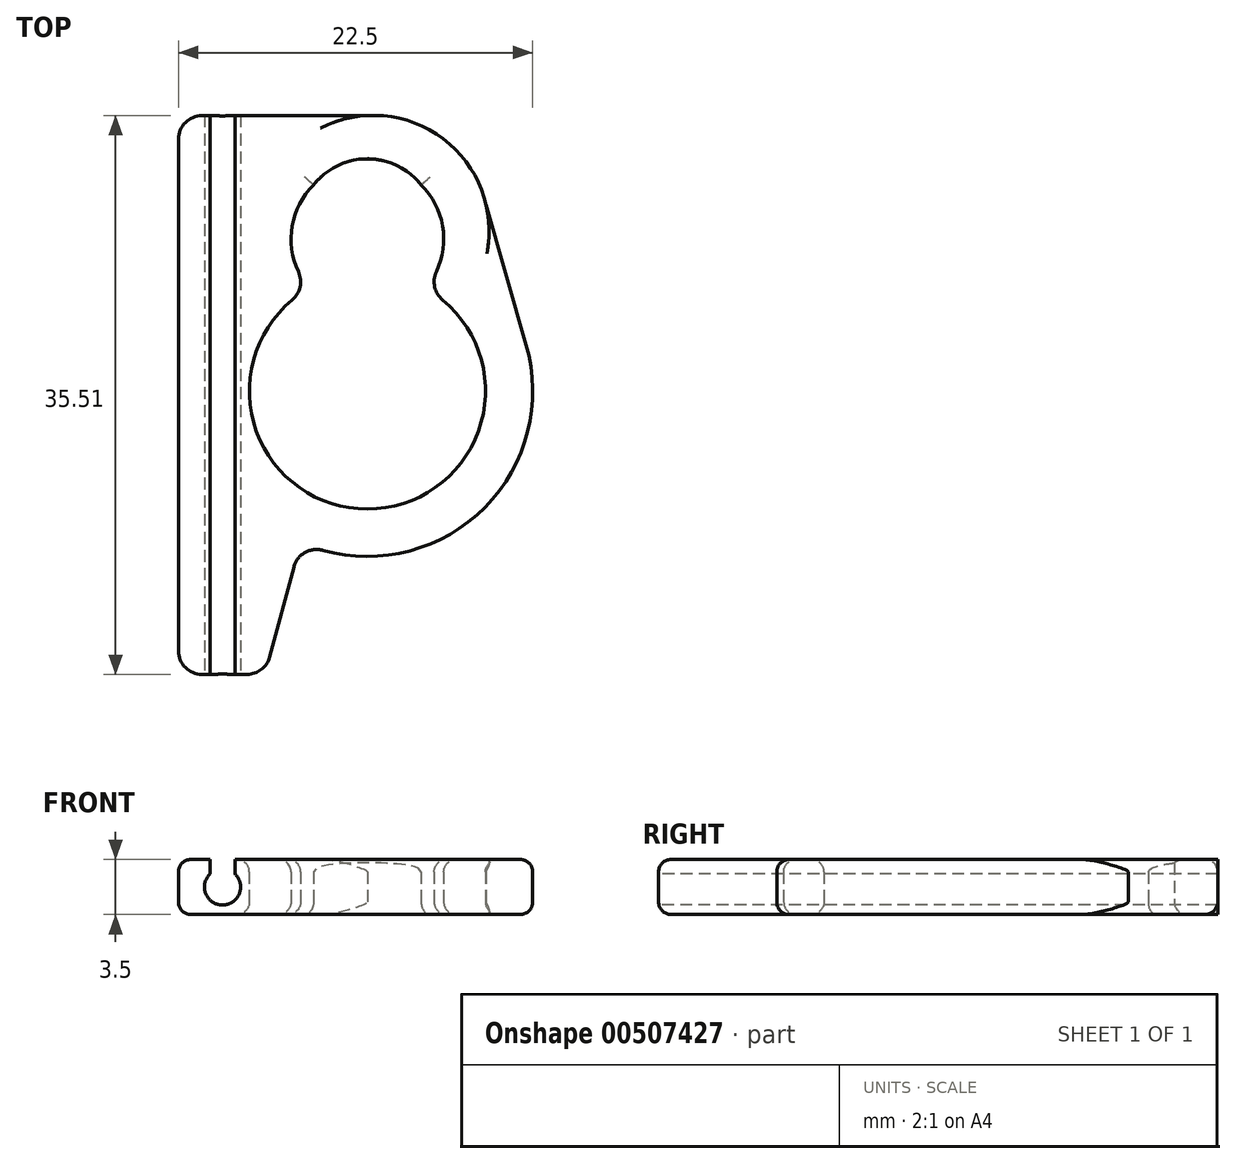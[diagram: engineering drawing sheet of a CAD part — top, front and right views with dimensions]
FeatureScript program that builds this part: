
annotation { "Feature Type Name" : "Feature", "Feature Type Description" : "" }
export const myFeature = defineFeature(function(context is Context, id is Id, definition is map)
    precondition{}
    {
        {
            var Q0;
            Q0=qCreatedBy(makeId("Top.planeOp"),FACE);
            var sketch = newSketch(context, id + "F0", { "sketchPlane" : qUnion([Q0])});
            skArc(sketch, "E0", {"start": v(-3.7, 6.52) * mm, "mid": v(0, -7.5) * mm, "end": v(3.7, 6.52) * mm});
            skArc(sketch, "E1", {"start": v(3.7, 6.52) * mm, "mid": v(0, 14.5) * mm, "end": v(-3.7, 6.52) * mm});
            skArc(sketch, "E2.0", {"start": v(7.54, 11.84) * mm, "mid": v(4.71, 15.93) * mm, "end": v(0, 17.5) * mm});
            skArc(sketch, "E2.1", {"start": v(-4.25, -9.6) * mm, "mid": v(6.91, -7.9) * mm, "end": v(10.08, 2.93) * mm});
            skPoint(sketch, "E3.endSnap0", {"position": v(0, -7.5) * mm});
            skLineSegment(sketch, "E4.MirrorCS", {"start": v(10.08, 2.93) * mm, "end": v(7.54, 11.84) * mm});
            skArc(sketch, "E5.MirrorCS", {"start": v(0, 17.5) * mm, "mid": v(4.8, 16.04) * mm, "end": v(7.54, 11.84) * mm});
            skArc(sketch, "E6.MirrorCS", {"start": v(-2.47, 6.82) * mm, "mid": v(0, 14.75) * mm, "end": v(2.47, 6.82) * mm});
            skLineSegment(sketch, "E7", {"start": v(0, 17.5) * mm, "end": v(-12, 17.5) * mm});
            skLineSegment(sketch, "E8", {"start": v(-12, 17.5) * mm, "end": v(-12, -18) * mm});
            skLineSegment(sketch, "E9", {"start": v(-12, -18) * mm, "end": v(-6.5, -18) * mm});
            skLineSegment(sketch, "E10", {"start": v(-6.5, -18) * mm, "end": v(-4.25, -9.6) * mm});
            skSolve(sketch);
        }
        {
            var Q0;
            Q0=qSketchRegion(id+"F0",true);
            extrude(context, id + "F1", {"entities" : qUnion([Q0]), "depth" : 3.5 * mm});
        }
        {
            var Q0;
            Q0=makeQuery(id+"F1.opExtrude","SWEPT_EDGE",EDGE,{"disambiguationData":[OSD([sQuery(id+"F0.wireOp",EDGE,"E9"),sQuery(id+"F0.wireOp",EDGE,"E10")])]});
            var Q1;
            Q1=makeQuery(id+"F1.opExtrude","SWEPT_EDGE",EDGE,{"disambiguationData":[OSD([sQuery(id+"F0.wireOp",EDGE,"E8"),sQuery(id+"F0.wireOp",EDGE,"E9")])]});
            var Q2;
            Q2=makeQuery(id+"F1.opExtrude","SWEPT_EDGE",EDGE,{"disambiguationData":[OSD([sQuery(id+"F0.wireOp",EDGE,"E2.1"),sQuery(id+"F0.wireOp",EDGE,"E10")])]});
            var Q3;
            {var subQ0=sQuery(id+"F0.wireOp",EDGE,"E6.MirrorCS");var subQ1=sQuery(id+"F0.wireOp",EDGE,"E0");Q3=makeQuery(id+"F1.opExtrude","SWEPT_EDGE",EDGE,{"disambiguationData":[OSD([subQ1,subQ0]),TDD([makeQuery(id+"F0.imprint","INTERSECT",VERTEX,{"disambiguationData":[OD(0.0)],"derivedFrom":[subQ1,subQ0]})])]});}
            var Q4;
            {var subQ0=sQuery(id+"F0.wireOp",EDGE,"E6.MirrorCS");var subQ1=sQuery(id+"F0.wireOp",EDGE,"E0");Q4=makeQuery(id+"F1.opExtrude","SWEPT_EDGE",EDGE,{"disambiguationData":[OSD([subQ1,subQ0]),TDD([makeQuery(id+"F0.imprint","INTERSECT",VERTEX,{"disambiguationData":[OD(1.0)],"derivedFrom":[subQ1,subQ0]})])]});}
            var Q5;
            Q5=makeQuery(id+"F1.opExtrude","SWEPT_EDGE",EDGE,{"disambiguationData":[OSD([sQuery(id+"F0.wireOp",EDGE,"E7"),sQuery(id+"F0.wireOp",EDGE,"E8")])]});
            var Q6;
            {var subQ0=sQuery(id+"F0.wireOp",EDGE,"E1");var subQ1=sQuery(id+"F0.wireOp",EDGE,"E0");Q6=makeQuery(id+"F1.opExtrude","SWEPT_EDGE",EDGE,{"disambiguationData":[OSD([subQ1,subQ0]),TDD([makeQuery(id+"F0.imprint","INTERSECT",VERTEX,{"disambiguationData":[OD(0.0)],"derivedFrom":[subQ1,subQ0]})])]});}
            var Q7;
            {var subQ0=sQuery(id+"F0.wireOp",EDGE,"E1");var subQ1=sQuery(id+"F0.wireOp",EDGE,"E0");Q7=makeQuery(id+"F1.opExtrude","SWEPT_EDGE",EDGE,{"disambiguationData":[OSD([subQ1,subQ0]),TDD([makeQuery(id+"F0.imprint","INTERSECT",VERTEX,{"disambiguationData":[OD(1.0)],"derivedFrom":[subQ1,subQ0]})])]});}
            fillet(context, id + "F2", {"entities" : qUnion([Q0, Q1, Q2, Q3, Q4, Q5, Q6, Q7]), "radius" : 1.5 * mm, "tangentPropagation" : true, "allowEdgeOverflow" : false});
        }
        {
            var Q0;
            Q0=makeQuery(id+"F1.opExtrude","CAP_EDGE",EDGE,{"disambiguationData":[OSD([sQuery(id+"F0.wireOp",EDGE,"E8")])],"isStart":false});
            var Q1;
            Q1=makeQuery(id+"F1.opExtrude","CAP_EDGE",EDGE,{"disambiguationData":[OSD([sQuery(id+"F0.wireOp",EDGE,"E0")])],"isStart":false});
            var Q2;
            Q2=makeQuery(id+"F1.opExtrude","CAP_EDGE",EDGE,{"disambiguationData":[OSD([sQuery(id+"F0.wireOp",EDGE,"E4.MirrorCS")])],"isStart":true});
            var Q3;
            Q3=makeQuery(id+"F1.opExtrude","CAP_EDGE",EDGE,{"disambiguationData":[OSD([sQuery(id+"F0.wireOp",EDGE,"E6.MirrorCS")])],"isStart":true});
            var Q4;
            Q4=makeQuery(id+"F1.opExtrude","CAP_EDGE",EDGE,{"disambiguationData":[OSD([sQuery(id+"F0.wireOp",EDGE,"E9")])],"isStart":true});
            var Q5;
            Q5=makeQuery(id+"F1.opExtrude","CAP_EDGE",EDGE,{"disambiguationData":[OSD([sQuery(id+"F0.wireOp",EDGE,"E0")])],"isStart":true});
            fillet(context, id + "F3", {"entities" : qUnion([Q0, Q1, Q2, Q3, Q4, Q5]), "radius" : 0.8 * mm, "tangentPropagation" : true, "allowEdgeOverflow" : false});
        }
        {
            var Q0;
            Q0=makeQuery(id+"F1.opExtrude","SWEPT_FACE",FACE,{"disambiguationData":[OSD([sQuery(id+"F0.wireOp",EDGE,"E9")])]});
            var sketch = newSketch(context, id + "F4", { "sketchPlane" : qUnion([Q0])});
            skArc(sketch, "E11", {"start": v(-10, 2.58) * mm, "mid": v(-9.2, 0.6) * mm, "end": v(-8.4, 2.58) * mm});
            skLineSegment(sketch, "E12.bottom", {"start": v(-8.4, 5.64) * mm, "end": v(-10, 5.64) * mm});
            skLineSegment(sketch, "E12.left", {"start": v(-8.4, 5.64) * mm, "end": v(-8.4, 2.58) * mm});
            skLineSegment(sketch, "E12.right", {"start": v(-10, 5.64) * mm, "end": v(-10, 2.58) * mm});
            skPoint(sketch, "E12.top.end.orphan", {"position": v(-10, -2.14) * mm});
            skPoint(sketch, "E12.top.start.orphan", {"position": v(-8.4, -2.14) * mm});
            skLineSegment(sketch, "E13", {"start": v(-9.2, 1.75) * mm, "end": v(-9.2, 4.67) * mm, "construction": true});
            skSolve(sketch);
        }
        {
            var Q0;
            Q0=qSketchRegion(id+"F4",true);
            var Q1;
            Q1=makeQuery(id+"F1.opExtrude","SWEPT_FACE",FACE,{"disambiguationData":[OSD([sQuery(id+"F0.wireOp",EDGE,"E7")])]});
            extrude(context, id + "F5", {"entities" : qUnion([Q0]), "operationType" : NewBodyOperationType.REMOVE, "endBound" : BoundingType.UP_TO_SURFACE, "oppositeDirection" : true, "endBoundEntityFace" : qUnion([Q1]), "depth" : 25 * mm});
        }
    });
